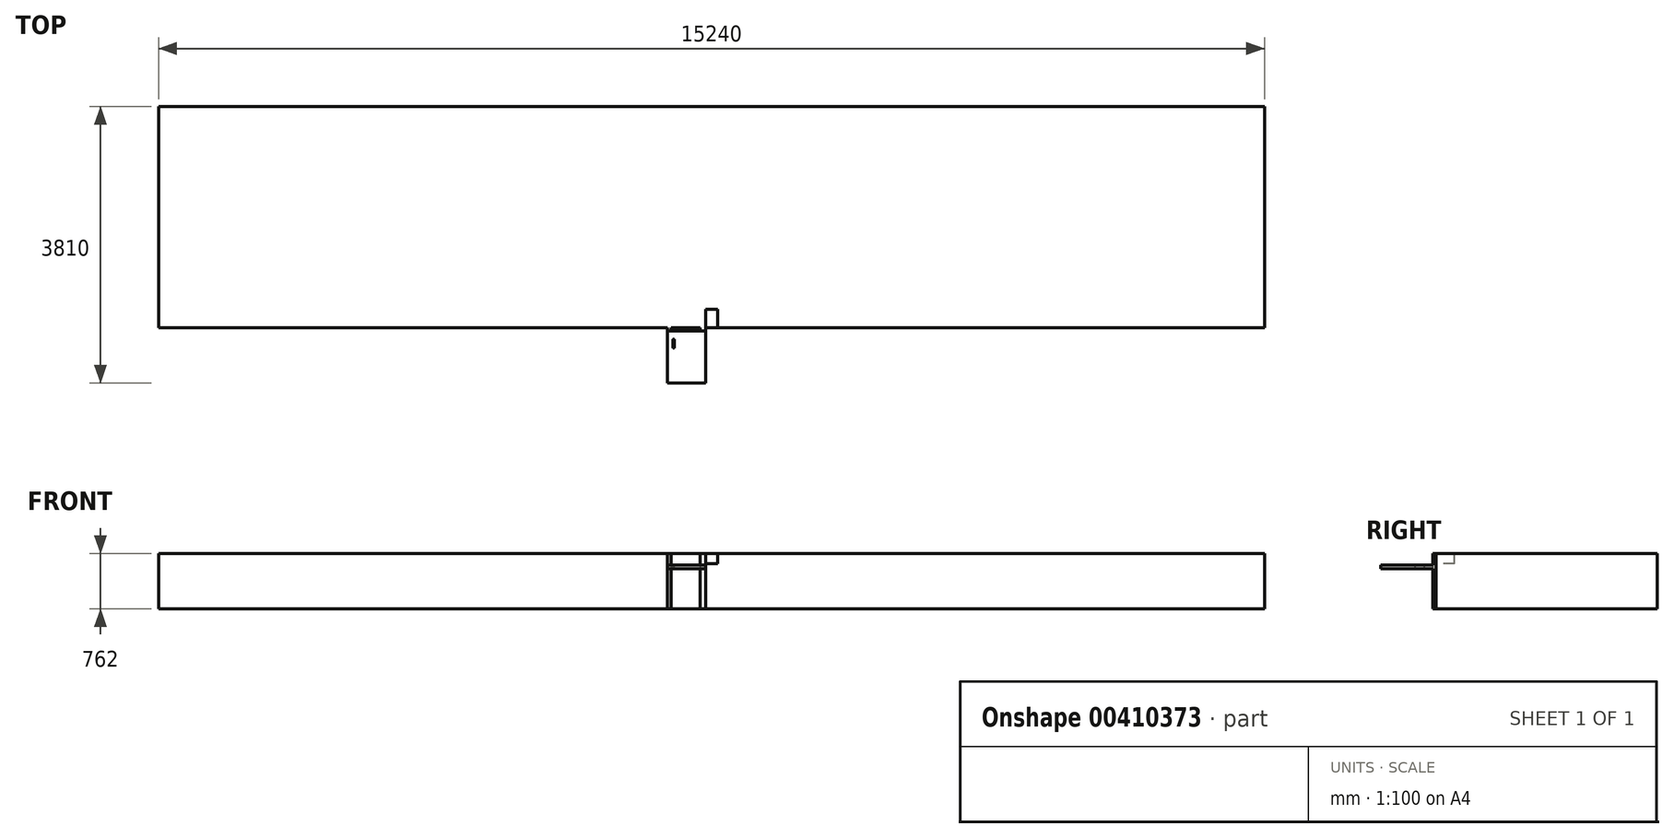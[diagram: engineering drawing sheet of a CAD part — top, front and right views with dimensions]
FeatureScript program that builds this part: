
annotation { "Feature Type Name" : "Feature", "Feature Type Description" : "" }
export const myFeature = defineFeature(function(context is Context, id is Id, definition is map)
    precondition{}
    {
        {
            var Q0;
            Q0=qCreatedBy(makeId("Top.planeOp"),FACE);
            var sketch = newSketch(context, id + "F0", { "sketchPlane" : qUnion([Q0])});
            skLineSegment(sketch, "E0.bottom", {"start": v(7620, 1524) * mm, "end": v(-7620, 1524) * mm});
            skLineSegment(sketch, "E0.top", {"start": v(7620, -1524) * mm, "end": v(-7620, -1524) * mm});
            skLineSegment(sketch, "E0.left", {"start": v(7620, 1524) * mm, "end": v(7620, -1524) * mm});
            skLineSegment(sketch, "E0.right", {"start": v(-7620, 1524) * mm, "end": v(-7620, -1524) * mm});
            skPoint(sketch, "E0.middle", {"position": v(0, 0) * mm});
            skSolve(sketch);
        }
        {
            var Q0;
            Q0 = qSketchRegion(id + "F0", true);
            extrude(context, id + "F1", {"entities" : qUnion([Q0]), "depth" : 762 * mm});
        }
        {
            var Q0;
            Q0=makeQuery(id+"F1.opExtrude","CAP_FACE",FACE,{"disambiguationData":[OSD([sQuery(id+"F0.wireOp",EDGE,"E0.bottom"),sQuery(id+"F0.wireOp",EDGE,"E0.top"),sQuery(id+"F0.wireOp",EDGE,"E0.left"),sQuery(id+"F0.wireOp",EDGE,"E0.right")])],"isStart":false});
            var sketch = newSketch(context, id + "F2", { "sketchPlane" : qUnion([Q0])});
            skLineSegment(sketch, "E1.bottom", {"start": v(82.55, -1270) * mm, "end": v(-82.55, -1270) * mm});
            skLineSegment(sketch, "E1.top", {"start": v(82.55, -1524) * mm, "end": v(-82.55, -1524) * mm});
            skLineSegment(sketch, "E1.left", {"start": v(82.55, -1270) * mm, "end": v(82.55, -1524) * mm});
            skLineSegment(sketch, "E1.right", {"start": v(-82.55, -1270) * mm, "end": v(-82.55, -1524) * mm});
            skPoint(sketch, "E1.middle", {"position": v(0, -1397) * mm});
            skSolve(sketch);
        }
        {
            var Q0;
            Q0 = qSketchRegion(id + "F2", true);
            extrude(context, id + "F3", {"entities" : qUnion([Q0]), "operationType" : NewBodyOperationType.REMOVE, "oppositeDirection" : true, "depth" : 139.7 * mm});
        }
        {
            var Q0;
            Q0=makeQuery(id+"F1.opExtrude","SWEPT_FACE",FACE,{"disambiguationData":[OSD([sQuery(id+"F0.wireOp",EDGE,"E0.top")])]});
            var sketch = newSketch(context, id + "F4", { "sketchPlane" : qUnion([Q0])});
            skLineSegment(sketch, "E2.bottom", {"start": v(-82.55, 762) * mm, "end": v(-158.75, 762) * mm});
            skLineSegment(sketch, "E2.top", {"start": v(-82.55, 0) * mm, "end": v(-158.75, 0) * mm});
            skLineSegment(sketch, "E2.left", {"start": v(-82.55, 762) * mm, "end": v(-82.55, 0) * mm});
            skLineSegment(sketch, "E2.right", {"start": v(-158.75, 762) * mm, "end": v(-158.75, 0) * mm});
            skSolve(sketch);
        }
        {
            var Q0;
            Q0 = qSketchRegion(id + "F4", true);
            extrude(context, id + "F5", {"entities" : qUnion([Q0]), "operationType" : NewBodyOperationType.ADD, "depth" : 44.45 * mm});
        }
        {
            var Q0;
            Q0=makeQuery(id+"F5.opExtrude","CAP_FACE",FACE,{"disambiguationData":[OSD([sQuery(id+"F4.wireOp",EDGE,"E2.bottom"),sQuery(id+"F4.wireOp",EDGE,"E2.top"),sQuery(id+"F4.wireOp",EDGE,"E2.left"),sQuery(id+"F4.wireOp",EDGE,"E2.right")])],"isStart":false});
            var sketch = newSketch(context, id + "F6", { "sketchPlane" : qUnion([Q0])});
            skLineSegment(sketch, "E3.bottom", {"start": v(-604.84, 600.08) * mm, "end": v(-82.55, 600.08) * mm});
            skLineSegment(sketch, "E3.top", {"start": v(-604.84, 549.28) * mm, "end": v(-82.55, 549.28) * mm});
            skLineSegment(sketch, "E3.left", {"start": v(-604.84, 600.08) * mm, "end": v(-604.84, 549.28) * mm});
            skLineSegment(sketch, "E3.right", {"start": v(-82.55, 600.08) * mm, "end": v(-82.55, 549.28) * mm});
            skSolve(sketch);
        }
        {
            var Q0;
            Q0 = qSketchRegion(id + "F6", true);
            extrude(context, id + "F7", {"entities" : qUnion([Q0]), "operationType" : NewBodyOperationType.ADD, "depth" : 717.55 * mm});
        }
        {
            var Q0;
            {var subQ0=sQuery(id+"F0.wireOp",EDGE,"E0.right");var subQ2=sQuery(id+"F0.wireOp",EDGE,"E0.top");Q0=makeQuery(id+"F5.boolean.opBoolean","SPLIT",FACE,{"disambiguationData":[TD([makeQuery(id+"F1.opExtrude","SWEPT_FACE",FACE,{"disambiguationData":[OSD([subQ0])]})])],"derivedFrom":makeQuery(id+"F1.opExtrude","SWEPT_FACE",FACE,{"disambiguationData":[OSD([subQ2])]})});}
            var sketch = newSketch(context, id + "F8", { "sketchPlane" : qUnion([Q0])});
            skLineSegment(sketch, "E4.bottom", {"start": v(-604.84, 762) * mm, "end": v(-554.04, 762) * mm});
            skLineSegment(sketch, "E4.top", {"start": v(-604.84, 0) * mm, "end": v(-554.04, 0) * mm});
            skLineSegment(sketch, "E4.left", {"start": v(-604.84, 762) * mm, "end": v(-604.84, 0) * mm});
            skLineSegment(sketch, "E4.right", {"start": v(-554.04, 762) * mm, "end": v(-554.04, 0) * mm});
            skSolve(sketch);
        }
        {
            var Q0;
            Q0 = qSketchRegion(id + "F8", true);
            extrude(context, id + "F9", {"entities" : qUnion([Q0]), "operationType" : NewBodyOperationType.ADD, "depth" : 44.45 * mm});
        }
        {
            var Q0;
            Q0=makeQuery(id+"F7.opExtrude","SWEPT_FACE",FACE,{"disambiguationData":[OSD([sQuery(id+"F6.wireOp",EDGE,"E3.bottom")])]});
            var sketch = newSketch(context, id + "F10", { "sketchPlane" : qUnion([Q0])});
            skLineSegment(sketch, "E5.left", {"start": v(-531.81, -1692.28) * mm, "end": v(-531.81, -1793.88) * mm});
            skLineSegment(sketch, "E5.right", {"start": v(-511.17, -1692.28) * mm, "end": v(-511.17, -1793.88) * mm});
            skArc(sketch, "E6", {"start": v(-511.17, -1692.28) * mm, "mid": v(-521.5, -1681.96) * mm, "end": v(-531.81, -1692.28) * mm});
            skArc(sketch, "E7", {"start": v(-531.81, -1793.88) * mm, "mid": v(-521.5, -1804.2) * mm, "end": v(-511.17, -1793.88) * mm});
            skSolve(sketch);
        }
        {
            var Q0;
            Q0 = qSketchRegion(id + "F10", true);
            extrude(context, id + "F11", {"entities" : qUnion([Q0]), "operationType" : NewBodyOperationType.REMOVE, "endBound" : BoundingType.UP_TO_NEXT, "oppositeDirection" : true, "depth" : 25.4 * mm});
        }
    });
